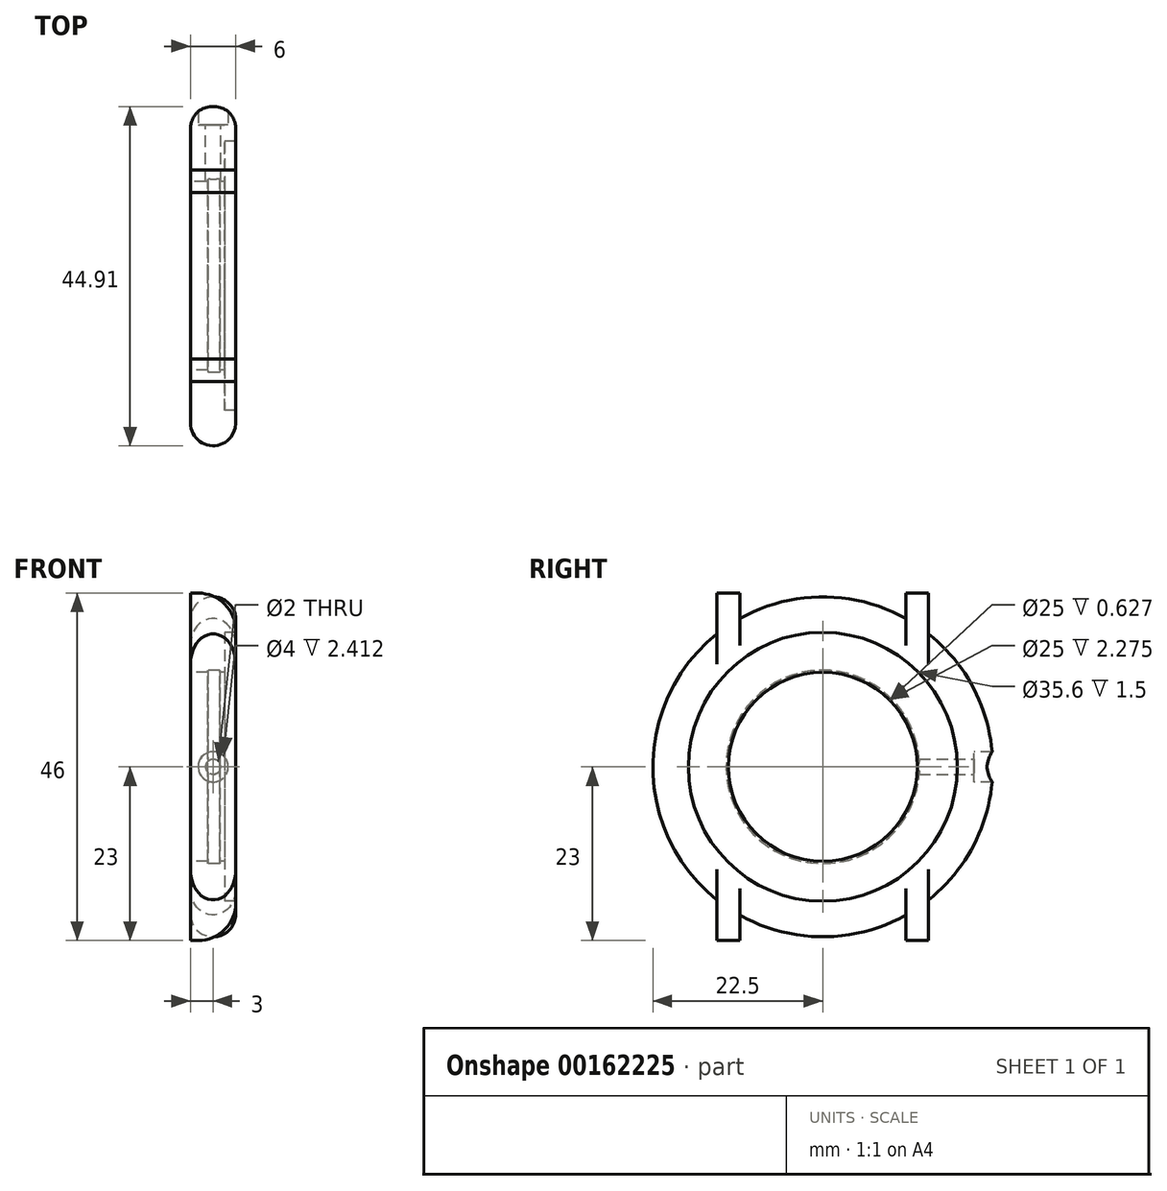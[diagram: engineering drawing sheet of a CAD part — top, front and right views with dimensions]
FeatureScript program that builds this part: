
annotation { "Feature Type Name" : "Feature", "Feature Type Description" : "" }
export const myFeature = defineFeature(function(context is Context, id is Id, definition is map)
    precondition{}
    {
        {
            var Q0;
            Q0=qCreatedBy(makeId("Front.planeOp"),FACE);
            var sketch = newSketch(context, id + "F0", { "sketchPlane" : qUnion([Q0])});
            skLineSegment(sketch, "E0", {"start": v(-3, 19.5) * mm, "end": v(-3, 12.5) * mm});
            skLineSegment(sketch, "E1", {"start": v(-3, 12.5) * mm, "end": v(-0.72, 12.5) * mm});
            skLineSegment(sketch, "E2", {"start": v(1.5, 12.5) * mm, "end": v(1.5, 17.8) * mm});
            skLineSegment(sketch, "E3", {"start": v(1.5, 17.8) * mm, "end": v(3, 17.8) * mm});
            skLineSegment(sketch, "E4", {"start": v(3, 17.8) * mm, "end": v(3, 19.5) * mm});
            skLineSegment(sketch, "E5", {"start": v(0.87, 12.5) * mm, "end": v(0.87, 12.8) * mm});
            skLineSegment(sketch, "E6", {"start": v(0.87, 12.8) * mm, "end": v(-0.72, 12.8) * mm});
            skLineSegment(sketch, "E7", {"start": v(-0.72, 12.8) * mm, "end": v(-0.72, 12.5) * mm});
            skLineSegment(sketch, "E8.trimOffspring", {"start": v(0.87, 12.5) * mm, "end": v(1.5, 12.5) * mm});
            skArc(sketch, "E9", {"start": v(3, 19.5) * mm, "mid": v(0, 22.5) * mm, "end": v(-3, 19.5) * mm});
            skLineSegment(sketch, "E10", {"start": v(0, 0) * mm, "end": v(27.78, 0) * mm});
            skSolve(sketch);
        }
        {
            var Q0;
            Q0 = qSketchRegion(id + "F0", true);
            var Q1;
            Q1=sQuery(id+"F0.wireOp",EDGE,"E10");
            revolve(context, id + "F1", {"entities" : qUnion([Q0]), "axis" : qUnion([Q1]), "revolveType" : RevolveType.TWO_DIRECTIONS, "angle" : 270 * degree, "angleBack" : 90 * degree});
        }
        {
            var Q0;
            Q0=qCreatedBy(makeId("Front.planeOp"),FACE);
            var sketch = newSketch(context, id + "F2", { "sketchPlane" : qUnion([Q0])});
            skPoint(sketch, "E11", {"position": v(0, 0) * mm});
            skSolve(sketch);
        }
        {
            var Q0;
            Q0=sQuery(id+"F2.wireOp",VERTEX,"E11");
            var Q1;
            Q1=makeQuery(id+"F1.opRevolve","SWEPT_BODY",BODY,{"disambiguationData":[OSD([sQuery(id+"F0.wireOp",EDGE,"E0"),sQuery(id+"F0.wireOp",EDGE,"E1"),sQuery(id+"F0.wireOp",EDGE,"E2"),sQuery(id+"F0.wireOp",EDGE,"E3"),sQuery(id+"F0.wireOp",EDGE,"E4"),sQuery(id+"F0.wireOp",EDGE,"E5"),sQuery(id+"F0.wireOp",EDGE,"E6"),sQuery(id+"F0.wireOp",EDGE,"E7"),sQuery(id+"F0.wireOp",EDGE,"E8.trimOffspring"),sQuery(id+"F0.wireOp",EDGE,"E9")])]});
            hole(context, id + "F3", {"style" : HoleStyle.SIMPLE, "endStyle" : HoleEndStyle.THROUGH, "holeDiameter" : 2 * mm, "isTappedThrough" : true, "tappedDepth" : 12 * mm, "tapClearance" : 3, "locations" : qUnion([Q0]), "scope" : qUnion([Q1])});
        }
        {
            var Q0;
            Q0=qCreatedBy(makeId("Top.planeOp"),FACE);
            cPlane(context, id + "F4", {"entities" : qUnion([Q0]), "cplaneType" : CPlaneType.OFFSET, "offset" : 20 * mm, "oppositeDirection" : true, "width" : 150 * mm, "height" : 150 * mm});
        }
        {
            var Q0;
            Q0=qCreatedBy(id+"F4.planeOp",FACE);
            var sketch = newSketch(context, id + "F5", { "sketchPlane" : qUnion([Q0])});
            skLineSegment(sketch, "E12.bottom", {"start": v(3, 14) * mm, "end": v(-3, 14) * mm});
            skLineSegment(sketch, "E12.top", {"start": v(3, 11) * mm, "end": v(-3, 11) * mm});
            skLineSegment(sketch, "E12.left", {"start": v(3, 14) * mm, "end": v(3, 11) * mm});
            skLineSegment(sketch, "E12.right", {"start": v(-3, 14) * mm, "end": v(-3, 11) * mm});
            skLineSegment(sketch, "E13.bottom", {"start": v(3, -11) * mm, "end": v(-3, -11) * mm});
            skLineSegment(sketch, "E13.top", {"start": v(3, -14) * mm, "end": v(-3, -14) * mm});
            skLineSegment(sketch, "E13.left", {"start": v(3, -11) * mm, "end": v(3, -14) * mm});
            skLineSegment(sketch, "E13.right", {"start": v(-3, -11) * mm, "end": v(-3, -14) * mm});
            skSolve(sketch);
        }
        {
            var Q0;
            Q0 = qSketchRegion(id + "F5", true);
            var Q1;
            Q1=makeQuery(id+"F1.opRevolve","SWEPT_FACE",FACE,{"disambiguationData":[OSD([sQuery(id+"F0.wireOp",EDGE,"E9")])]});
            extrude(context, id + "F6", {"entities" : qUnion([Q0]), "operationType" : NewBodyOperationType.ADD, "endBound" : BoundingType.UP_TO_SURFACE, "endBoundEntityFace" : qUnion([Q1]), "depth" : 25 * mm, "hasSecondDirection" : true, "secondDirectionOppositeDirection" : true, "secondDirectionDepth" : 3 * mm});
        }
        {
            var Q0;
            Q0=makeQuery(id+"F6.opExtrude","CAP_EDGE",EDGE,{"disambiguationData":[OSD([sQuery(id+"F5.wireOp",EDGE,"E13.left")])],"isStart":true});
            var Q1;
            Q1=makeQuery(id+"F6.opExtrude","CAP_EDGE",EDGE,{"disambiguationData":[OSD([sQuery(id+"F5.wireOp",EDGE,"E12.left")])],"isStart":true});
            fillet(context, id + "F7", {"entities" : qUnion([Q0, Q1]), "radius" : 5 * mm, "tangentPropagation" : true, "allowEdgeOverflow" : false});
        }
        {
            var Q0;
            Q0=makeQuery(id+"F1.opRevolve","SWEPT_BODY",BODY,{"disambiguationData":[OSD([sQuery(id+"F0.wireOp",EDGE,"E0"),sQuery(id+"F0.wireOp",EDGE,"E1"),sQuery(id+"F0.wireOp",EDGE,"E2"),sQuery(id+"F0.wireOp",EDGE,"E3"),sQuery(id+"F0.wireOp",EDGE,"E4"),sQuery(id+"F0.wireOp",EDGE,"E5"),sQuery(id+"F0.wireOp",EDGE,"E6"),sQuery(id+"F0.wireOp",EDGE,"E7"),sQuery(id+"F0.wireOp",EDGE,"E8.trimOffspring"),sQuery(id+"F0.wireOp",EDGE,"E9")])]});
            var Q1;
            Q1=qCreatedBy(makeId("Top.planeOp"),FACE);
            mirror(context, id + "F8", {"operationType" : NewBodyOperationType.ADD, "entities" : qUnion([Q0]), "mirrorPlane" : qUnion([Q1])});
        }
        {
            var Q0;
            Q0=qCreatedBy(makeId("Front.planeOp"),FACE);
            var sketch = newSketch(context, id + "F9", { "sketchPlane" : qUnion([Q0])});
            skCircle(sketch, "E14", {"center": v(0, 0) * mm, "radius": 2 * mm});
            skSolve(sketch);
        }
        {
            var Q0;
            Q0 = qSketchRegion(id + "F9", true);
            extrude(context, id + "F10", {"entities" : qUnion([Q0]), "operationType" : NewBodyOperationType.REMOVE, "oppositeDirection" : true, "depth" : 27 * mm, "hasSecondDirection" : true, "secondDirectionOppositeDirection" : true, "secondDirectionDepth" : 20 * mm});
        }
    });
